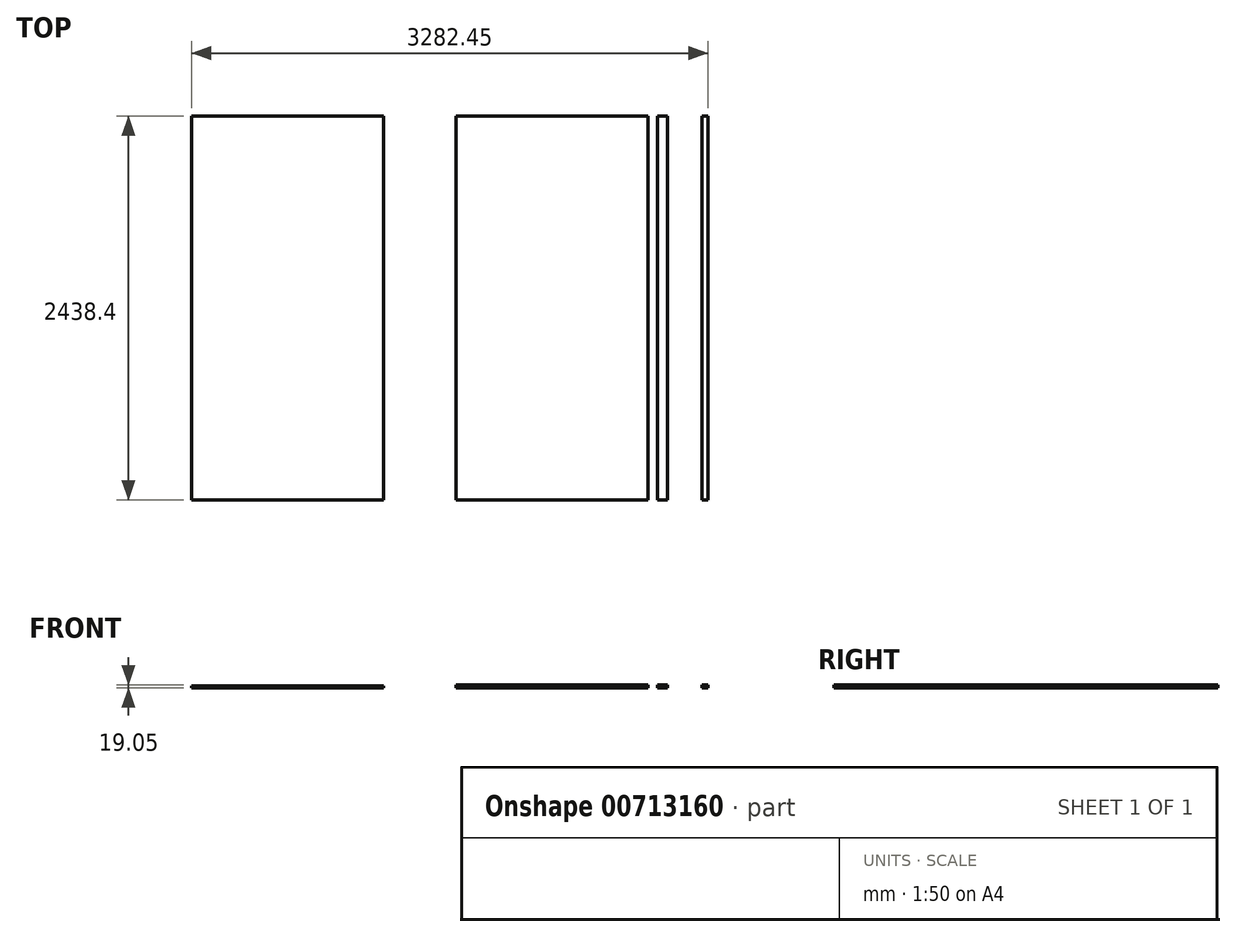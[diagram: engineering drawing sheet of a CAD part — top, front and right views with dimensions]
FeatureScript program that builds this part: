
annotation { "Feature Type Name" : "Feature", "Feature Type Description" : "" }
export const myFeature = defineFeature(function(context is Context, id is Id, definition is map)
    precondition{}
    {
        {
            var Q0;
            Q0=qCreatedBy(makeId("Top.planeOp"),FACE);
            var sketch = newSketch(context, id + "F0", { "sketchPlane" : qUnion([Q0])});
            skLineSegment(sketch, "E0.bottom", {"start": v(0, 0) * mm, "end": v(-1219.2, 0) * mm});
            skLineSegment(sketch, "E0.top", {"start": v(0, 2438.4) * mm, "end": v(-1219.2, 2438.4) * mm});
            skLineSegment(sketch, "E0.left", {"start": v(0, 0) * mm, "end": v(0, 2438.4) * mm});
            skLineSegment(sketch, "E0.right", {"start": v(-1219.2, 0) * mm, "end": v(-1219.2, 2438.4) * mm});
            skLineSegment(sketch, "E1.bottom", {"start": v(-1679.62, 0) * mm, "end": v(-2898.82, 0) * mm});
            skLineSegment(sketch, "E1.top", {"start": v(-1679.62, 2438.4) * mm, "end": v(-2898.82, 2438.4) * mm});
            skLineSegment(sketch, "E1.left", {"start": v(-1679.62, 0) * mm, "end": v(-1679.62, 2438.4) * mm});
            skLineSegment(sketch, "E1.right", {"start": v(-2898.82, 0) * mm, "end": v(-2898.82, 2438.4) * mm});
            skSolve(sketch);
        }
        {
            var Q0;
            Q0=makeQuery(id+"F0.imprint","IMPRINT",FACE,{"disambiguationData":[TD([[makeQuery(id+"F0.imprint","IMPRINT",EDGE,{"derivedFrom":sQuery(id+"F0.wireOp",EDGE,"E0.bottom")}),-1.0]])]});
            extrude(context, id + "F1", {"entities" : qUnion([Q0]), "depth" : 18.26 * mm, "offsetDistance" : 25.4 * mm});
        }
        {
            var Q0;
            Q0=qCreatedBy(makeId("Top.planeOp"),FACE);
            var sketch = newSketch(context, id + "F2", { "sketchPlane" : qUnion([Q0])});
            skLineSegment(sketch, "E2.bottom", {"start": v(61.25, 0) * mm, "end": v(124.75, 0) * mm});
            skLineSegment(sketch, "E2.top", {"start": v(61.25, 2438.4) * mm, "end": v(124.75, 2438.4) * mm});
            skLineSegment(sketch, "E2.left", {"start": v(61.25, 0) * mm, "end": v(61.25, 2438.4) * mm});
            skLineSegment(sketch, "E2.right", {"start": v(124.75, 0) * mm, "end": v(124.75, 2438.4) * mm});
            skLineSegment(sketch, "E3.bottom", {"start": v(345.53, 0) * mm, "end": v(383.63, 0) * mm});
            skLineSegment(sketch, "E3.top", {"start": v(345.53, 2438.4) * mm, "end": v(383.63, 2438.4) * mm});
            skLineSegment(sketch, "E3.left", {"start": v(345.53, 0) * mm, "end": v(345.53, 2438.4) * mm});
            skLineSegment(sketch, "E3.right", {"start": v(383.63, 0) * mm, "end": v(383.63, 2438.4) * mm});
            skSolve(sketch);
        }
        {
            var Q0;
            Q0 = qSketchRegion(id + "F2", true);
            extrude(context, id + "F3", {"entities" : qUnion([Q0]), "depth" : 19.05 * mm, "offsetDistance" : 25.4 * mm});
        }
        {
            var Q0;
            Q0=makeQuery(id+"F0.imprint","IMPRINT",FACE,{"disambiguationData":[TD([[makeQuery(id+"F0.imprint","IMPRINT",EDGE,{"derivedFrom":sQuery(id+"F0.wireOp",EDGE,"E1.bottom")}),-1.0]])]});
            extrude(context, id + "F4", {"entities" : qUnion([Q0]), "depth" : 12.7 * mm, "offsetDistance" : 25.4 * mm});
        }
    });
